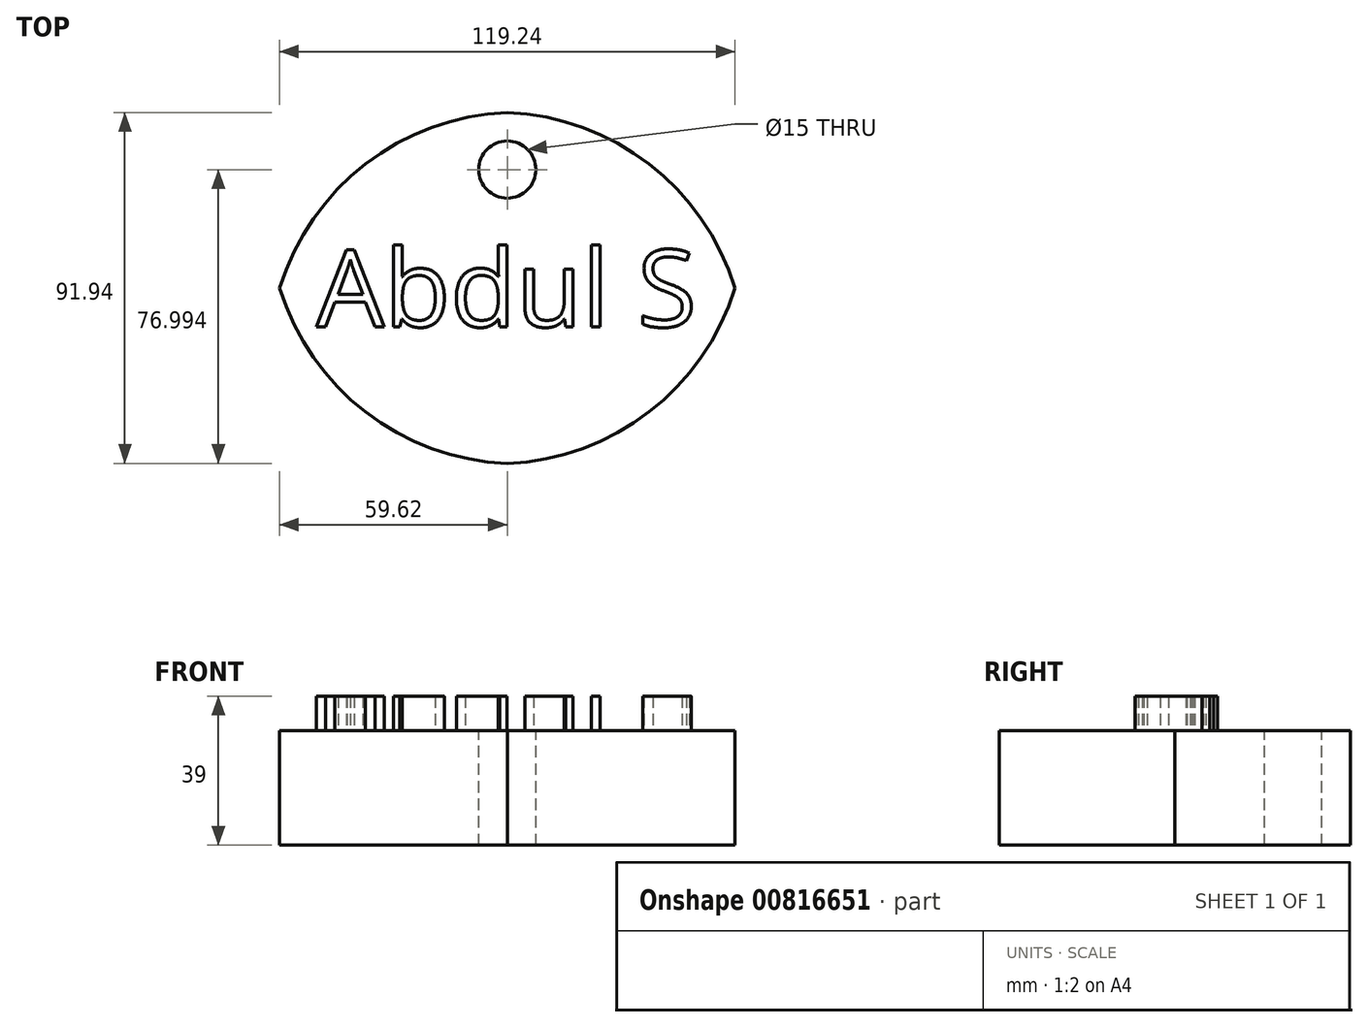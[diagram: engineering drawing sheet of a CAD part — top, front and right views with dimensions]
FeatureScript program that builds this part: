
annotation { "Feature Type Name" : "Feature", "Feature Type Description" : "" }
export const myFeature = defineFeature(function(context is Context, id is Id, definition is map)
    precondition{}
    {
        {
            var Q0;
            Q0=qCreatedBy(makeId("Top.planeOp"),FACE);
            var sketch = newSketch(context, id + "F0", { "sketchPlane" : qUnion([Q0])});
            skLineSegment(sketch, "E0.bottom", {"start": v(62.5, 46.02) * mm, "end": v(-62.5, 46.02) * mm});
            skLineSegment(sketch, "E0.top", {"start": v(62.5, -46.02) * mm, "end": v(-62.5, -46.02) * mm});
            skLineSegment(sketch, "E0.left", {"start": v(62.5, 46.02) * mm, "end": v(62.5, -46.02) * mm});
            skLineSegment(sketch, "E0.right", {"start": v(-62.5, 46.02) * mm, "end": v(-62.5, -46.02) * mm});
            skPoint(sketch, "E0.middle", {"position": v(0, 0) * mm});
            skSolve(sketch);
        }
        {
            var Q0;
            Q0=makeQuery(id+"F0.imprint","IMPRINT",FACE,{"disambiguationData":[TD([[makeQuery(id+"F0.imprint","IMPRINT",EDGE,{"derivedFrom":sQuery(id+"F0.wireOp",EDGE,"E0.bottom")}),1.0]])]});
            extrude(context, id + "F1", {"entities" : qUnion([Q0]), "depth" : 30 * mm, "offsetDistance" : 25 * mm});
        }
        {
            var Q0;
            Q0=makeQuery(id+"F1.opExtrude","CAP_FACE",FACE,{"disambiguationData":[OSD([sQuery(id+"F0.wireOp",EDGE,"E0.bottom"),sQuery(id+"F0.wireOp",EDGE,"E0.top"),sQuery(id+"F0.wireOp",EDGE,"E0.left"),sQuery(id+"F0.wireOp",EDGE,"E0.right")])],"isStart":false});
            var sketch = newSketch(context, id + "F2", { "sketchPlane" : qUnion([Q0])});
            skText(sketch, "E1", { "text": "Abdul S", "fontName": "OpenSans-Regular.ttf"});
            skLineSegment(sketch, "E2", {"start": v(62.5, 0) * mm, "end": v(50, 0) * mm, "construction": true});
            skLineSegment(sketch, "E3", {"start": v(-50, 0) * mm, "end": v(-62.5, 0) * mm, "construction": true});
            skPoint(sketch, "E3.startSnap0", {"position": v(-62.5, 0) * mm});
            skLineSegment(sketch, "E4", {"start": v(0, 46.02) * mm, "end": v(0, 10.14) * mm, "construction": true});
            skLineSegment(sketch, "E5", {"start": v(0, 10.14) * mm, "end": v(0, -46.02) * mm, "construction": true});
            const initialGuessF2  = {"E1": [-0.05, -0.01014, 1, 0, 0.02028]};
            skSetInitialGuess(sketch, initialGuessF2);
            skSolve(sketch);
        }
        {
            var Q0;
            Q0 = qSketchRegion(id + "F2", true);
            extrude(context, id + "F3", {"entities" : qUnion([Q0]), "operationType" : NewBodyOperationType.ADD, "depth" : 9 * mm, "offsetDistance" : 25 * mm});
        }
        {
            var Q0;
            {var subQ0=sQuery(id+"F0.wireOp",EDGE,"E0.left");var subQ1=sQuery(id+"F0.wireOp",EDGE,"E0.bottom");var subQ2=sQuery(id+"F0.wireOp",EDGE,"E0.right");var subQ3=sQuery(id+"F0.wireOp",EDGE,"E0.top");Q0=makeQuery(id+"F3.boolean.opBoolean","SPLIT",FACE,{"disambiguationData":[TD([makeQuery(id+"F1.opExtrude","SWEPT_FACE",FACE,{"disambiguationData":[OSD([subQ1])]})])],"derivedFrom":makeQuery(id+"F1.opExtrude","CAP_FACE",FACE,{"disambiguationData":[OSD([subQ1,subQ3,subQ0,subQ2])],"isStart":false})});}
            var sketch = newSketch(context, id + "F4", { "sketchPlane" : qUnion([Q0])});
            skCircle(sketch, "E6", {"center": v(0, 31.02) * mm, "radius": 7.5 * mm});
            skLineSegment(sketch, "E7", {"start": v(0, 31.02) * mm, "end": v(0, 46.02) * mm});
            skSolve(sketch);
        }
        {
            var Q0;
            Q0 = qSketchRegion(id + "F4", true);
            extrude(context, id + "F5", {"entities" : qUnion([Q0]), "operationType" : NewBodyOperationType.REMOVE, "oppositeDirection" : true, "depth" : 128.6 * mm, "offsetDistance" : 25 * mm});
        }
        {
            var Q0;
            Q0=makeQuery(id+"F1.opExtrude","SWEPT_EDGE",EDGE,{"disambiguationData":[OSD([sQuery(id+"F0.wireOp",EDGE,"E0.bottom"),sQuery(id+"F0.wireOp",EDGE,"E0.left")])]});
            var Q1;
            Q1=makeQuery(id+"F1.opExtrude","SWEPT_EDGE",EDGE,{"disambiguationData":[OSD([sQuery(id+"F0.wireOp",EDGE,"E0.top"),sQuery(id+"F0.wireOp",EDGE,"E0.left")])]});
            var Q2;
            Q2=makeQuery(id+"F1.opExtrude","SWEPT_EDGE",EDGE,{"disambiguationData":[OSD([sQuery(id+"F0.wireOp",EDGE,"E0.top"),sQuery(id+"F0.wireOp",EDGE,"E0.right")])]});
            var Q3;
            Q3=makeQuery(id+"F1.opExtrude","SWEPT_EDGE",EDGE,{"disambiguationData":[OSD([sQuery(id+"F0.wireOp",EDGE,"E0.bottom"),sQuery(id+"F0.wireOp",EDGE,"E0.right")])]});
            fillet(context, id + "F6", {"entities" : qUnion([Q0, Q1, Q2, Q3]), "radius" : 65.18 * mm, "tangentPropagation" : true, "allowEdgeOverflow" : false});
        }
    });
